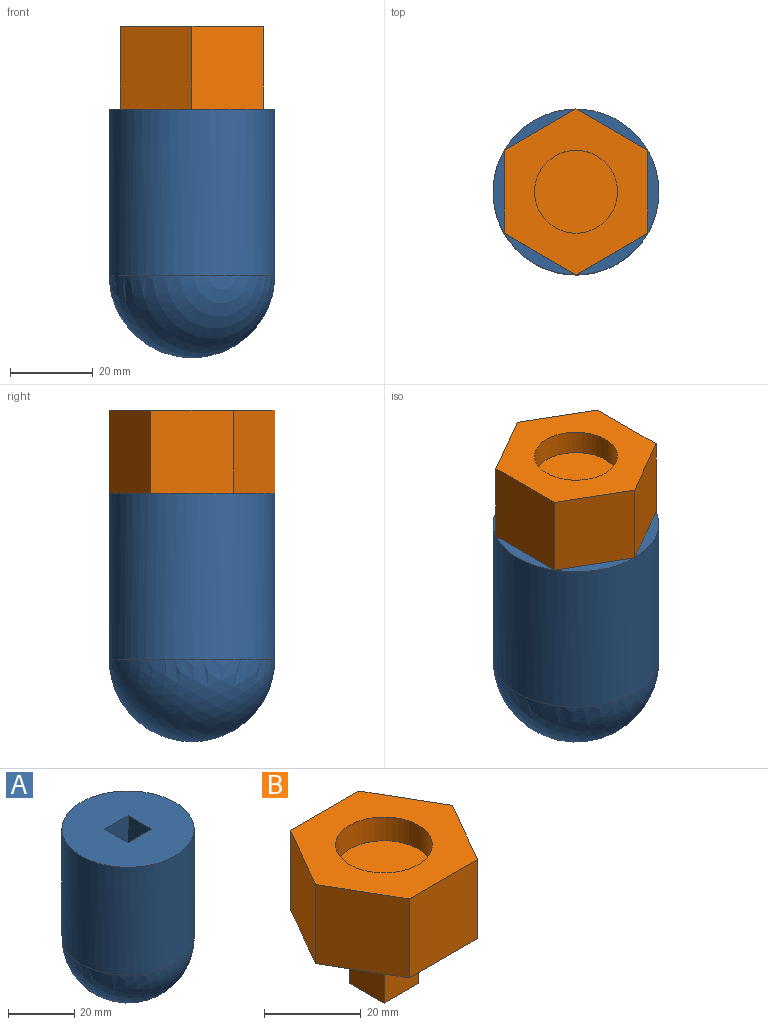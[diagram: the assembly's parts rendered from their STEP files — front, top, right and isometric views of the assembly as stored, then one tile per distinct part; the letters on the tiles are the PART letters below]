
ASSEMBLY  parts=2 mates=1
PART A: 8 faces, bbox 40x40x60 mm
  f0: plane 40x40mm, normal (0,0,1), area 1156.6mm2, adj f1,f2,f3,f4,f5
  f1: cylinder r=20mm len=40mm, axis (0,0,-1), area 5026.5mm2, adj f0,f7
  f2: plane 15x10mm, normal (0,1,0), area 150mm2, adj f0,f3,f5,f6
  f3: plane 15x10mm, normal (-1,0,0), area 150mm2, adj f0,f2,f4,f6
  f4: plane 15x10mm, normal (0,-1,0), area 150mm2, adj f0,f3,f5,f6
  f5: plane 15x10mm, normal (1,0,0), area 150mm2, adj f0,f2,f4,f6
  f6: plane 10x10mm, normal (0,0,1), area 100mm2, adj f2,f3,f4,f5
  f7: sphere r=20mm, area 2513.3mm2, adj f1
PART B: 15 faces, bbox 40x34.6x35 mm
  f0: plane 20x20mm, normal (0,-1,0), area 400mm2, adj f1,f5,f6,f7
  f1: plane 20x17.32mm, normal (0.87,-0.5,0), area 400mm2, adj f0,f2,f6,f7
  f2: plane 20x17.32mm, normal (0.87,0.5,0), area 400mm2, adj f1,f3,f6,f7
  f3: plane 20x20mm, normal (0,1,0), area 400mm2, adj f2,f4,f6,f7
  f4: plane 20x17.32mm, normal (-0.87,0.5,0), area 400mm2, adj f3,f5,f6,f7
  f5: plane 20x17.32mm, normal (-0.87,-0.5,0), area 400mm2, adj f0,f4,f6,f7
  f6: plane 40x34.64mm, normal (0,0,-1), area 939.2mm2, adj f0,f1,f2,f3,f4,f5,f10,f11
  f7: plane 40x34.64mm, normal (0,0,1), area 725.1mm2, adj f0,f1,f2,f3,f4,f5,f8
  f8: cylinder r=10mm len=20mm, axis (0,0,1), area 377mm2, adj f7,f9
  f9: plane 20x20mm, normal (0,0,1), area 314.2mm2, adj f8
  f10: plane 15x10mm, normal (0,1,0), area 150mm2, adj f6,f11,f13,f14
  f11: plane 15x10mm, normal (1,0,0), area 150mm2, adj f6,f10,f12,f14
  f12: plane 15x10mm, normal (0,-1,0), area 150mm2, adj f6,f11,f13,f14
  f13: plane 15x10mm, normal (-1,0,0), area 150mm2, adj f6,f10,f12,f14
  f14: plane 10x10mm, normal (0,0,-1), area 100mm2, adj f10,f11,f12,f13
PLACE A t=(35.57,4.3,-53.77)mm
PLACE B rot(axis=(0,0,-1),90deg) t=(35.57,4.3,6.23)mm
MATE fastened B.f8 <-> A.f1  axis (0,0,-1) through (35.57,4.3,-28.77)mm
